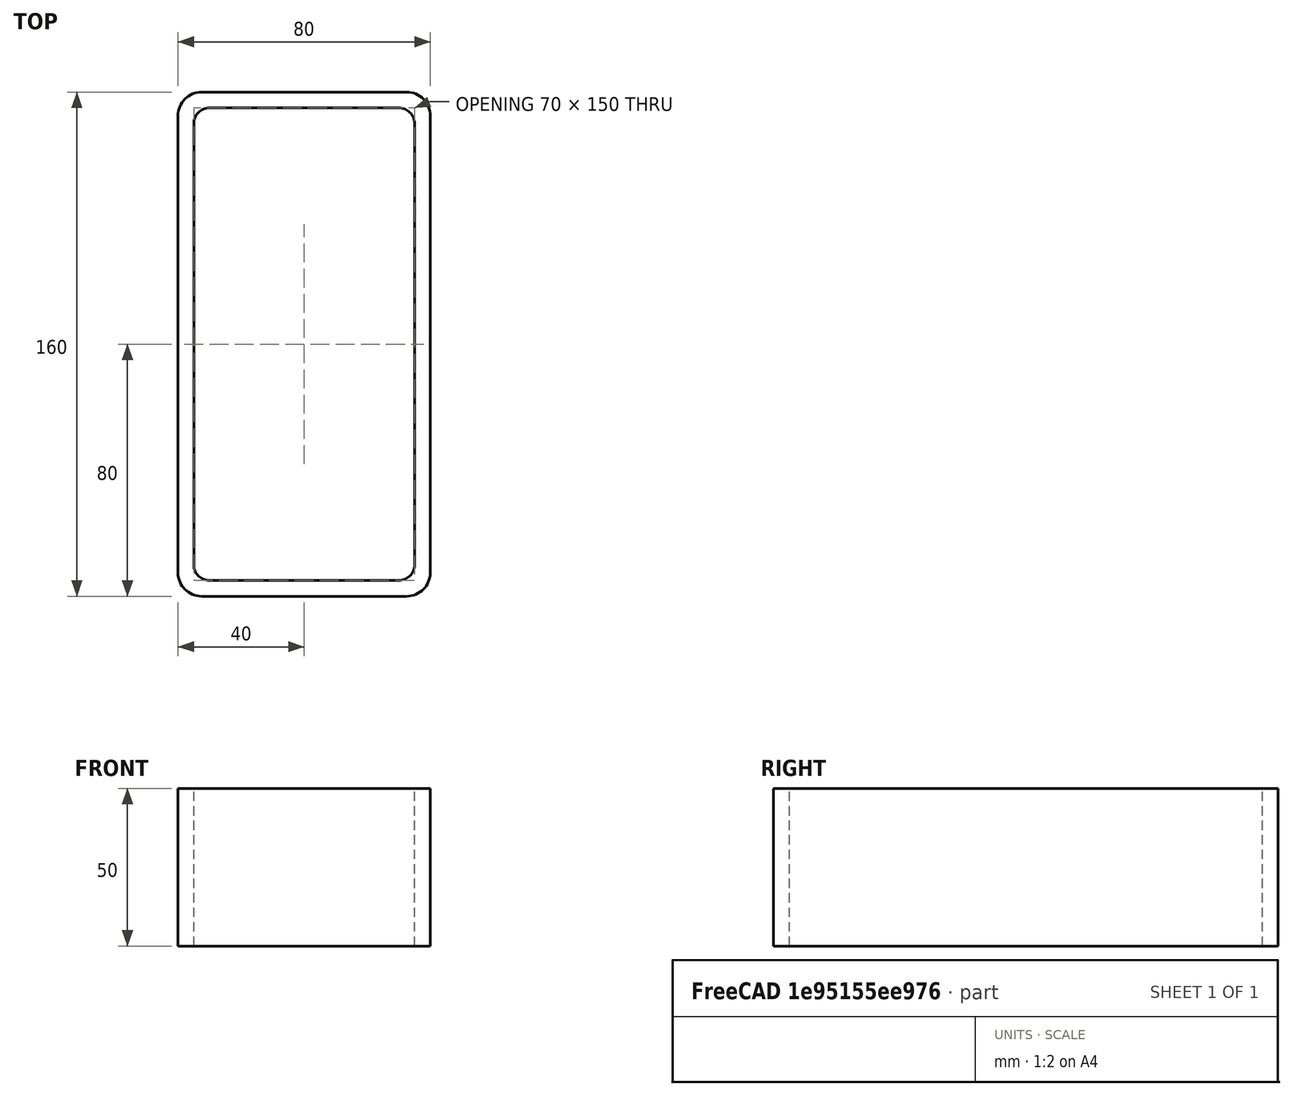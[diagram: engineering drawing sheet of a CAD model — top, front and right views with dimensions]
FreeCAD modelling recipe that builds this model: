
FCSTD DOCUMENT  (FreeCAD 0.15R4671 (Git))
Label: Rectangular hollow section 160x80x5 EN10219 S235JRH
License: All rights reserved
LicenseURL: http://en.wikipedia.org/wiki/All_rights_reserved
objects: Sketcher::SketchObject×1, Part::Extrusion×1
note: 2 computed .brp shape members not serialized (recipe doc carries the construction recipe); baked Part::Feature solids carry a one-line shape summary decoded from their .brp

FEATURE [Sketcher::SketchObject] Sketch
  sketch-geometry (16):
    g0: LineSegment StartX=-30 StartY=75 StartZ=0 EndX=30 EndY=75 EndZ=0
    g1: LineSegment StartX=35 StartY=70 StartZ=0 EndX=35 EndY=-70 EndZ=0
    g2: LineSegment StartX=30 StartY=-75 StartZ=0 EndX=-30 EndY=-75 EndZ=0
    g3: LineSegment StartX=-35 StartY=-70 StartZ=0 EndX=-35 EndY=70 EndZ=0
    g4: LineSegment StartX=-32.5 StartY=80 StartZ=0 EndX=32.5 EndY=80 EndZ=0
    g5: LineSegment StartX=40 StartY=72.5 StartZ=0 EndX=40 EndY=-72.5 EndZ=0
    g6: LineSegment StartX=32.5 StartY=-80 StartZ=0 EndX=-32.5 EndY=-80 EndZ=0
    g7: LineSegment StartX=-40 StartY=-72.5 StartZ=0 EndX=-40 EndY=72.5 EndZ=0
    g8: ArcOfCircle CenterX=-30 CenterY=70 CenterZ=0 NormalX=0 NormalY=0 NormalZ=1 Radius=5 StartAngle=1.5708 EndAngle=3.14159
    g9: ArcOfCircle CenterX=30 CenterY=70 CenterZ=0 NormalX=0 NormalY=0 NormalZ=1 Radius=5 StartAngle=0 EndAngle=1.5708
    g10: ArcOfCircle CenterX=30 CenterY=-70 CenterZ=0 NormalX=0 NormalY=0 NormalZ=1 Radius=5 StartAngle=4.71239 EndAngle=6.28319
    g11: ArcOfCircle CenterX=-30 CenterY=-70 CenterZ=0 NormalX=0 NormalY=0 NormalZ=1 Radius=5 StartAngle=3.14159 EndAngle=4.71239
    g12: ArcOfCircle CenterX=32.5 CenterY=72.5 CenterZ=0 NormalX=0 NormalY=0 NormalZ=1 Radius=7.5 StartAngle=0 EndAngle=1.5708
    g13: ArcOfCircle CenterX=32.5 CenterY=-72.5 CenterZ=0 NormalX=0 NormalY=0 NormalZ=1 Radius=7.5 StartAngle=4.71239 EndAngle=6.28319
    g14: ArcOfCircle CenterX=-32.5 CenterY=-72.5 CenterZ=0 NormalX=0 NormalY=0 NormalZ=1 Radius=7.5 StartAngle=3.14159 EndAngle=4.71239
    g15: ArcOfCircle CenterX=-32.5 CenterY=72.5 CenterZ=0 NormalX=0 NormalY=0 NormalZ=1 Radius=7.5 StartAngle=1.5708 EndAngle=3.14159
  constraints (36):
    c: Horizontal(g2)
    c: Vertical(g3)
    c: Horizontal(g6)
    c: Vertical(g7)
    c: Tangent(g3,g8) = 1.5708
    c: Tangent(g0,g8) = 1.5708
    c: Tangent(g0,g9) = 1.5708
    c: Tangent(g1,g9) = 1.5708
    c: Tangent(g1,g10) = 1.5708
    c: Tangent(g2,g10) = 1.5708
    c: Tangent(g2,g11) = 1.5708
    c: Tangent(g3,g11) = 1.5708
    c: Tangent(g4,g12) = 1.5708
    c: Tangent(g5,g12) = 1.5708
    c: Tangent(g5,g13) = 1.5708
    c: Tangent(g6,g13) = 1.5708
    c: Tangent(g6,g14) = 1.5708
    c: Tangent(g7,g14) = 1.5708
    c: Tangent(g7,g15) = 1.5708
    c: Tangent(g4,g15) = 1.5708
    c: Equal(g9,g8)
    c: Equal(g9,g11)
    c: Equal(g9,g10)
    c: Equal(g12,g15)
    c: Equal(g12,g14)
    c: Equal(g12,g13)
    c: Symmetric(g4,g6,g-1)
    c: Symmetric(g7,g5,g-2)
    c: DistanceY(g4,g6) = -160
    c: DistanceX(g7,g5) = 80
    c: Symmetric(g3,g1,g-2)
    c: Symmetric(g0,g2,g-1)
    c: DistanceY(g0,g4) = 5
    c: DistanceX(g5,g1) = -5
    c: Radius(g9) = 5
    c: Radius(g12) = 7.5
FEATURE [Part::Extrusion] Extrude  label="Rectangular hollow section 160x80x5 EN10219 S235JRH"
  Base = -> Sketch
  Dir = (0,0,50)
  Solid = true
